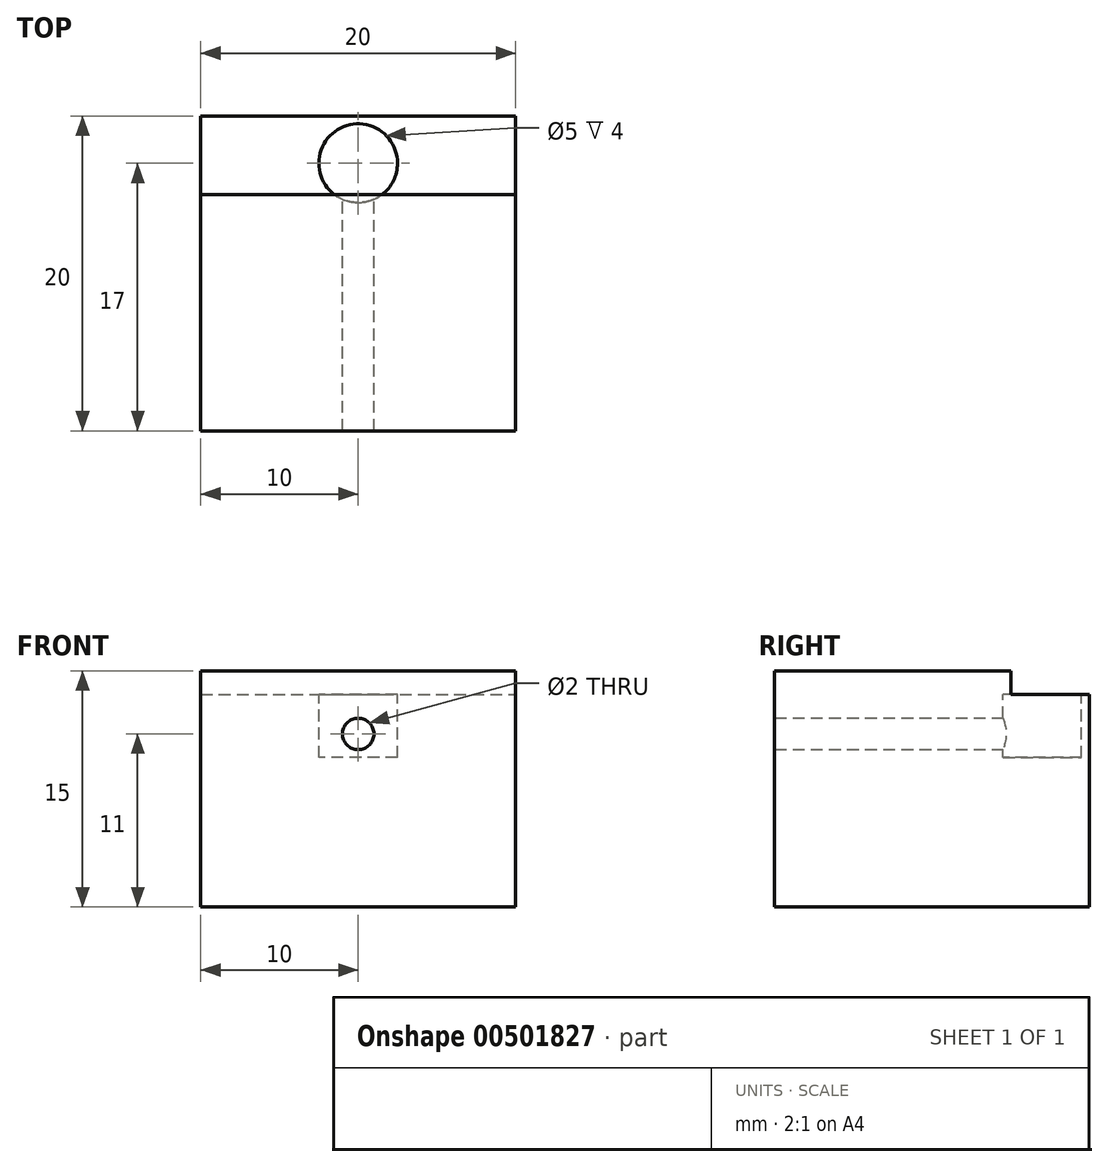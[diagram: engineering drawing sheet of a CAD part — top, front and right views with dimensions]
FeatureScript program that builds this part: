
annotation { "Feature Type Name" : "Feature", "Feature Type Description" : "" }
export const myFeature = defineFeature(function(context is Context, id is Id, definition is map)
    precondition{}
    {
        {
            var Q0;
            Q0=qCreatedBy(makeId("Top.planeOp"),FACE);
            var sketch = newSketch(context, id + "F0", { "sketchPlane" : qUnion([Q0])});
            skLineSegment(sketch, "E0.bottom", {"start": v(-10, 10) * mm, "end": v(10, 10) * mm});
            skLineSegment(sketch, "E0.top", {"start": v(-10, -10) * mm, "end": v(10, -10) * mm});
            skLineSegment(sketch, "E0.left", {"start": v(-10, 10) * mm, "end": v(-10, -10) * mm});
            skLineSegment(sketch, "E0.right", {"start": v(10, 10) * mm, "end": v(10, -10) * mm});
            skSolve(sketch);
        }
        {
            var Q0;
            Q0 = qSketchRegion(id + "F0", true);
            extrude(context, id + "F1", {"entities" : qUnion([Q0]), "depth" : 15 * mm});
        }
        {
            var Q0;
            Q0=makeQuery(id+"F1.opExtrude","CAP_FACE",FACE,{"disambiguationData":[OSD([sQuery(id+"F0.wireOp",EDGE,"E0.bottom"),sQuery(id+"F0.wireOp",EDGE,"E0.top"),sQuery(id+"F0.wireOp",EDGE,"E0.left"),sQuery(id+"F0.wireOp",EDGE,"E0.right")])],"isStart":false});
            var sketch = newSketch(context, id + "F2", { "sketchPlane" : qUnion([Q0])});
            skLineSegment(sketch, "E1.bottom", {"start": v(-25.59, 20.18) * mm, "end": v(24.6, 20.18) * mm});
            skLineSegment(sketch, "E1.top", {"start": v(-25.59, 5) * mm, "end": v(24.6, 5) * mm});
            skLineSegment(sketch, "E1.left", {"start": v(-25.59, 20.18) * mm, "end": v(-25.59, 5) * mm});
            skLineSegment(sketch, "E1.right", {"start": v(24.6, 20.18) * mm, "end": v(24.6, 5) * mm});
            skSolve(sketch);
        }
        {
            var Q0;
            Q0 = qSketchRegion(id + "F2", true);
            extrude(context, id + "F3", {"entities" : qUnion([Q0]), "operationType" : NewBodyOperationType.REMOVE, "oppositeDirection" : true, "depth" : 1.5 * mm});
        }
        {
            var Q0;
            Q0=makeQuery(id+"F3.boolean.opBoolean","COPY",FACE,{"derivedFrom":makeQuery(id+"F3.opExtrude","CAP_FACE",FACE,{"disambiguationData":[OSD([sQuery(id+"F2.wireOp",EDGE,"E1.bottom"),sQuery(id+"F2.wireOp",EDGE,"E1.top"),sQuery(id+"F2.wireOp",EDGE,"E1.left"),sQuery(id+"F2.wireOp",EDGE,"E1.right")])],"isStart":false})});
            var sketch = newSketch(context, id + "F4", { "sketchPlane" : qUnion([Q0])});
            skCircle(sketch, "E2", {"center": v(0, 7) * mm, "radius": 2.5 * mm});
            skSolve(sketch);
        }
        {
            var Q0;
            Q0 = qSketchRegion(id + "F4", true);
            extrude(context, id + "F5", {"entities" : qUnion([Q0]), "operationType" : NewBodyOperationType.REMOVE, "oppositeDirection" : true, "depth" : 4 * mm});
        }
        {
            var Q0;
            Q0=makeQuery(id+"F5.boolean.opBoolean","MERGE",FACE,{"derivedFrom":[makeQuery(id+"F3.boolean.opBoolean","COPY",FACE,{"derivedFrom":makeQuery(id+"F3.opExtrude","SWEPT_FACE",FACE,{"disambiguationData":[OSD([sQuery(id+"F2.wireOp",EDGE,"E1.top")])]})}),makeQuery(id+"F5.opExtrude","SWEPT_FACE",FACE,{"disambiguationData":[OSD([sQuery(id+"F4.wireOp",EDGE,"JtydVj79-Wteg-mX2V-DC7T-xMIQW8Yyjs52.top")])]})]});
            var sketch = newSketch(context, id + "F6", { "sketchPlane" : qUnion([Q0])});
            skCircle(sketch, "E3", {"center": v(0, 11) * mm, "radius": 1 * mm});
            skPoint(sketch, "E3.centerSnap0", {"position": v(0, 15) * mm});
            skSolve(sketch);
        }
        {
            var Q0;
            Q0 = qSketchRegion(id + "F6", true);
            extrude(context, id + "F7", {"entities" : qUnion([Q0]), "operationType" : NewBodyOperationType.REMOVE, "oppositeDirection" : true, "depth" : 25 * mm});
        }
    });
